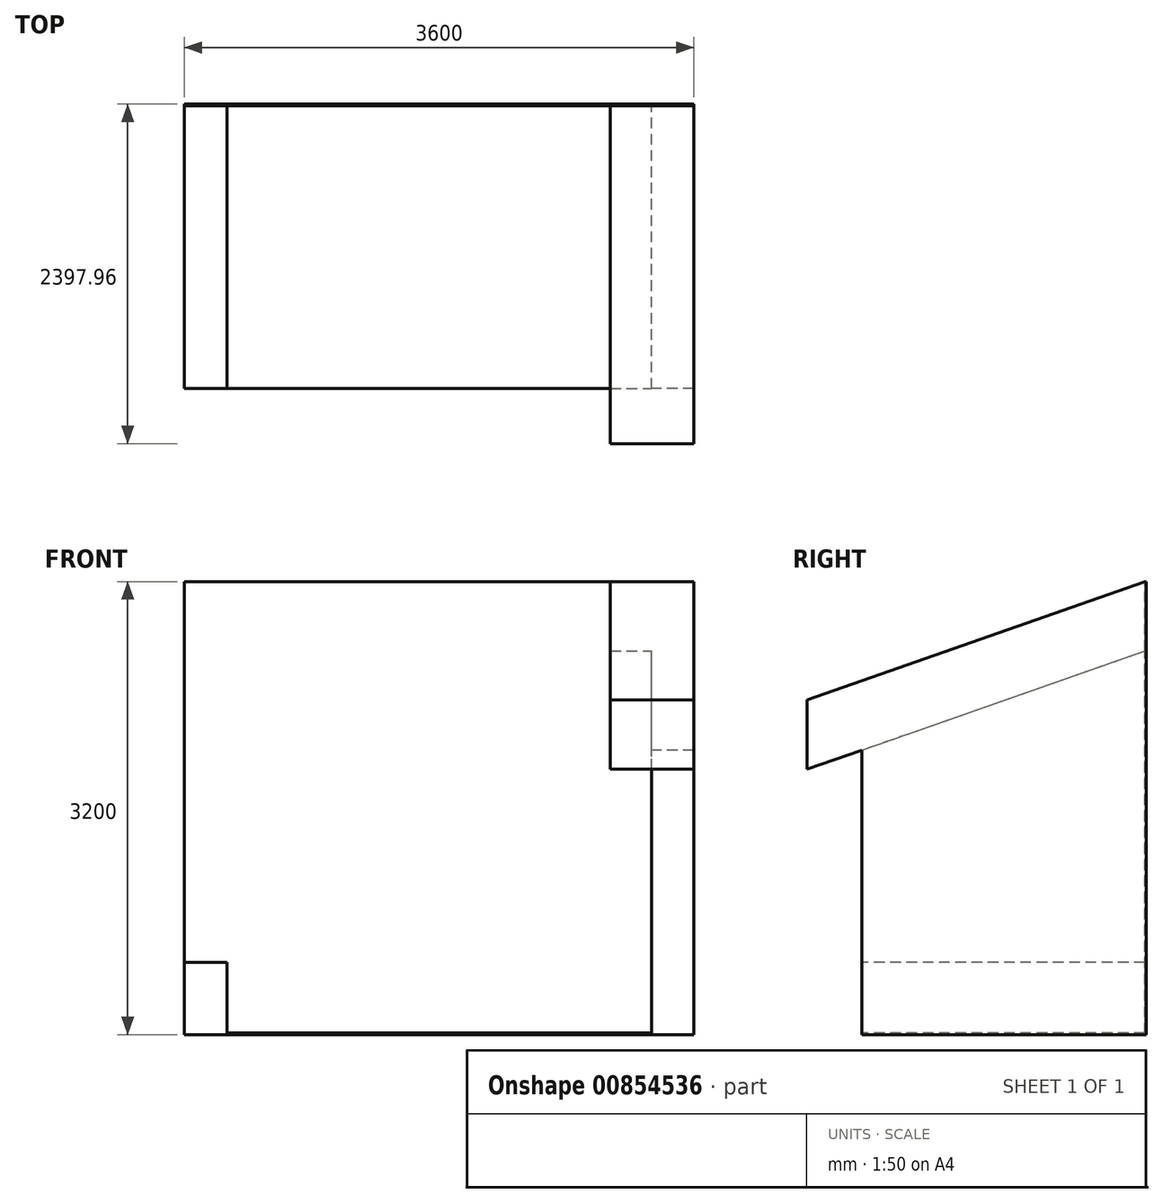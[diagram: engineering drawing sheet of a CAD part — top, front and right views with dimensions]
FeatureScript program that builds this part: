
annotation { "Feature Type Name" : "Feature", "Feature Type Description" : "" }
export const myFeature = defineFeature(function(context is Context, id is Id, definition is map)
    precondition{}
    {
        {
            var Q0;
            Q0=qCreatedBy(makeId("Front.planeOp"),FACE);
            var sketch = newSketch(context, id + "F0", { "sketchPlane" : qUnion([Q0])});
            skLineSegment(sketch, "E0.bottom", {"start": v(-3600, 500) * mm, "end": v(-3300, 500) * mm});
            skLineSegment(sketch, "E0.top", {"start": v(-3600, 0) * mm, "end": v(-3300, 0) * mm});
            skLineSegment(sketch, "E0.left", {"start": v(-3600, 500) * mm, "end": v(-3600, 0) * mm});
            skLineSegment(sketch, "E0.right", {"start": v(-3300, 500) * mm, "end": v(-3300, 0) * mm});
            skLineSegment(sketch, "E1.bottom", {"start": v(0, 0) * mm, "end": v(-300, 0) * mm});
            skLineSegment(sketch, "E1.top", {"start": v(0, 2000) * mm, "end": v(-300, 2000) * mm});
            skLineSegment(sketch, "E1.left", {"start": v(0, 0) * mm, "end": v(0, 2000) * mm});
            skLineSegment(sketch, "E1.right", {"start": v(-300, 0) * mm, "end": v(-300, 2000) * mm});
            skLineSegment(sketch, "E2.bottom", {"start": v(-3600, 0) * mm, "end": v(0, 0) * mm});
            skLineSegment(sketch, "E2.top", {"start": v(-3600, -10) * mm, "end": v(0, -10) * mm});
            skLineSegment(sketch, "E2.left", {"start": v(-3600, 0) * mm, "end": v(-3600, -10) * mm});
            skLineSegment(sketch, "E2.right", {"start": v(0, 0) * mm, "end": v(0, -10) * mm});
            skSolve(sketch);
        }
        {
            var Q0;
            Q0 = qSketchRegion(id + "F0", true);
            extrude(context, id + "F1", {"entities" : qUnion([Q0]), "oppositeDirection" : true, "depth" : 2000 * mm, "offsetDistance" : 25 * mm});
        }
        {
            var Q0;
            Q0=makeQuery(id+"F1.opExtrude","CAP_FACE",FACE,{"disambiguationData":[OSD([sQuery(id+"F0.wireOp",EDGE,"E0.bottom"),sQuery(id+"F0.wireOp",EDGE,"E0.left"),sQuery(id+"F0.wireOp",EDGE,"E0.right"),sQuery(id+"F0.wireOp",EDGE,"E1.top"),sQuery(id+"F0.wireOp",EDGE,"E1.left"),sQuery(id+"F0.wireOp",EDGE,"E1.right"),sQuery(id+"F0.wireOp",EDGE,"E2.bottom"),sQuery(id+"F0.wireOp",EDGE,"E2.top"),sQuery(id+"F0.wireOp",EDGE,"E2.left"),sQuery(id+"F0.wireOp",EDGE,"E2.right")])],"isStart":false});
            var sketch = newSketch(context, id + "F2", { "sketchPlane" : qUnion([Q0])});
            skLineSegment(sketch, "E3", {"start": v(3600, -10) * mm, "end": v(0, -10) * mm});
            skLineSegment(sketch, "E4", {"start": v(0, -10) * mm, "end": v(0, 3190) * mm});
            skLineSegment(sketch, "E5", {"start": v(3600, -10) * mm, "end": v(3600, 3190) * mm});
            skLineSegment(sketch, "E6", {"start": v(3600, 3190) * mm, "end": v(0, 3190) * mm});
            skSolve(sketch);
        }
        {
            var Q0;
            Q0 = qSketchRegion(id + "F2", true);
            extrude(context, id + "F3", {"entities" : qUnion([Q0]), "operationType" : NewBodyOperationType.ADD, "depth" : 10 * mm, "offsetDistance" : 25 * mm});
        }
        {
            var Q0;
            Q0=makeQuery(id+"F3.boolean.opBoolean","MERGE",FACE,{"derivedFrom":[makeQuery(id+"F1.opExtrude","SWEPT_FACE",FACE,{"disambiguationData":[OSD([sQuery(id+"F0.wireOp",EDGE,"E1.left"),sQuery(id+"F0.wireOp",EDGE,"E2.right")])]}),makeQuery(id+"F3.opExtrude","SWEPT_FACE",FACE,{"disambiguationData":[OSD([sQuery(id+"F2.wireOp",EDGE,"E4")])]})]});
            var sketch = newSketch(context, id + "F4", { "sketchPlane" : qUnion([Q0])});
            skLineSegment(sketch, "E7", {"start": v(0, 2000) * mm, "end": v(2000, 2700) * mm});
            skLineSegment(sketch, "E8", {"start": v(2000, 2700) * mm, "end": v(2000, 2000) * mm});
            skLineSegment(sketch, "E9", {"start": v(2000, 2000) * mm, "end": v(0, 2000) * mm});
            skSolve(sketch);
        }
        {
            var Q0;
            Q0 = qSketchRegion(id + "F4", true);
            extrude(context, id + "F5", {"entities" : qUnion([Q0]), "operationType" : NewBodyOperationType.ADD, "oppositeDirection" : true, "depth" : 300 * mm, "offsetDistance" : 25 * mm});
        }
        {
            var Q0;
            Q0=makeQuery(id+"F5.opExtrude","SWEPT_FACE",FACE,{"disambiguationData":[OSD([sQuery(id+"F4.wireOp",EDGE,"E7")])]});
            var sketch = newSketch(context, id + "F6", { "sketchPlane" : qUnion([Q0])});
            skLineSegment(sketch, "E10", {"start": v(0, 2779.66) * mm, "end": v(0, 249.66) * mm});
            skLineSegment(sketch, "E11", {"start": v(0, 249.66) * mm, "end": v(-590, 249.66) * mm});
            skLineSegment(sketch, "E12", {"start": v(-590, 249.66) * mm, "end": v(-590, 2779.66) * mm});
            skLineSegment(sketch, "E13", {"start": v(-590, 2779.66) * mm, "end": v(0, 2779.66) * mm});
            skSolve(sketch);
        }
        {
            var Q0;
            Q0 = qSketchRegion(id + "F6", true);
            var Q1;
            Q1=makeQuery(id+"F3.opExtrude","CAP_EDGE",EDGE,{"disambiguationData":[OSD([sQuery(id+"F2.wireOp",EDGE,"E4")])],"isStart":true});
            sweep(context, id + "F7", {"operationType" : NewBodyOperationType.ADD, "profiles" : qUnion([Q0]), "path" : qUnion([Q1])});
        }
    });
